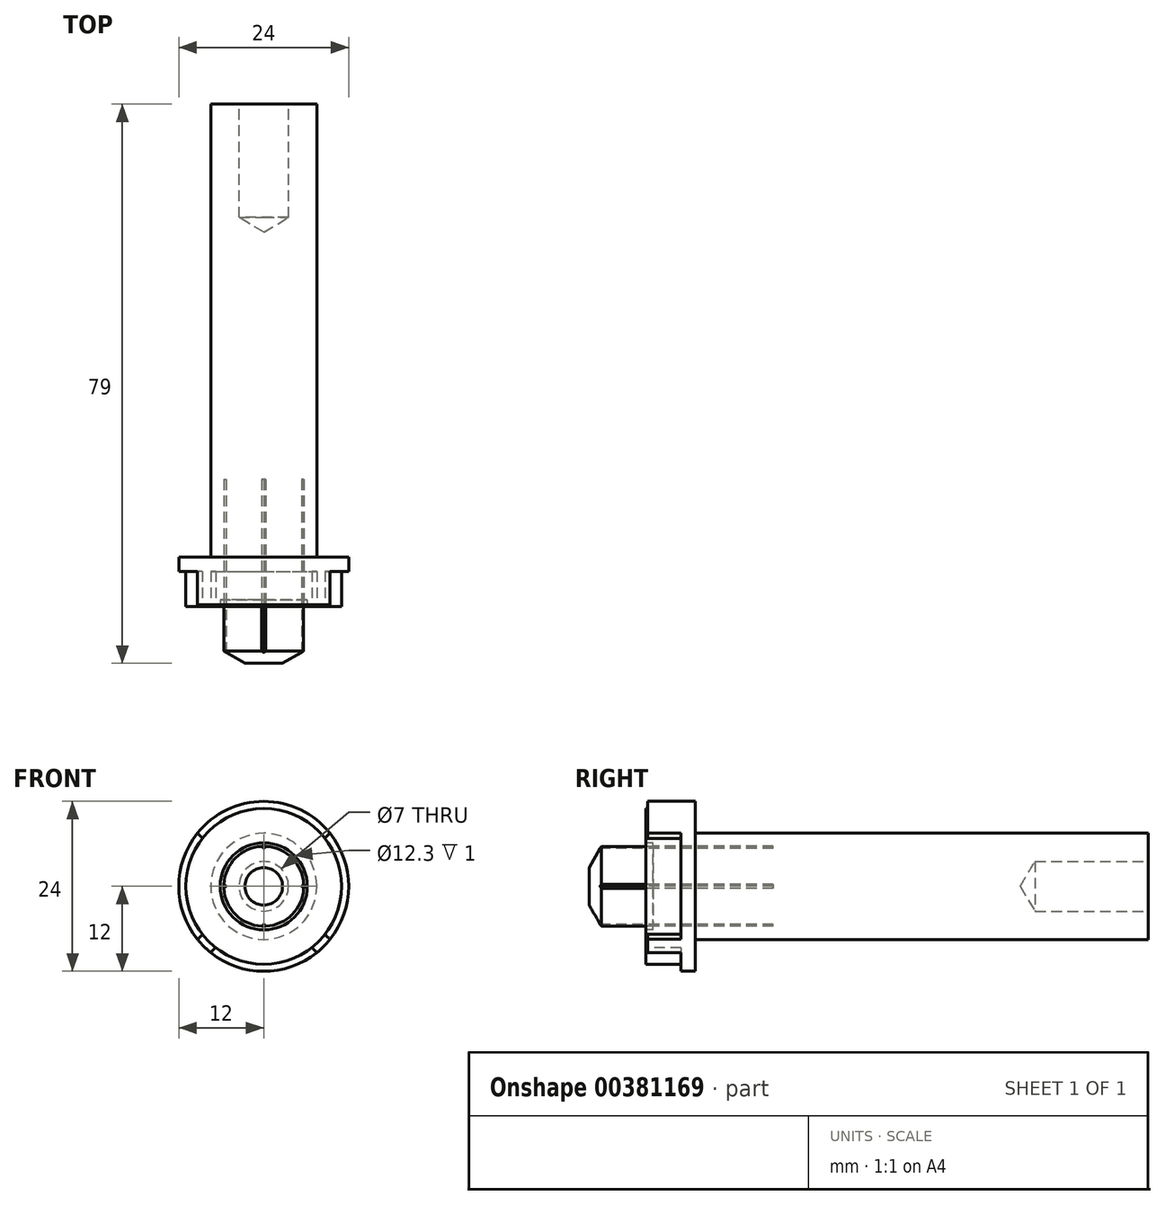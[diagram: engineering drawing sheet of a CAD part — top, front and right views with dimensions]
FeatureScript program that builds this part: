
annotation { "Feature Type Name" : "Feature", "Feature Type Description" : "" }
export const myFeature = defineFeature(function(context is Context, id is Id, definition is map)
    precondition{}
    {
        {
            var Q0;
            Q0=qCreatedBy(makeId("Front.planeOp"),FACE);
            var sketch = newSketch(context, id + "F0", { "sketchPlane" : qUnion([Q0])});
            skCircle(sketch, "E0", {"center": v(0, 0) * mm, "radius": 12 * mm});
            skSolve(sketch);
        }
        {
            var Q0;
            Q0=makeQuery(id+"F0.imprint","IMPRINT",FACE,{"disambiguationData":[TD([[makeQuery(id+"F0.imprint","IMPRINT",EDGE,{"derivedFrom":sQuery(id+"F0.wireOp",EDGE,"E0")}),1.0]])]});
            extrude(context, id + "F1", {"entities" : qUnion([Q0]), "depth" : 7 * mm});
        }
        {
            var Q0;
            Q0=makeQuery(id+"F1.opExtrude","CAP_FACE",FACE,{"disambiguationData":[OSD([sQuery(id+"F0.wireOp",EDGE,"E0")])],"isStart":true});
            var sketch = newSketch(context, id + "F2", { "sketchPlane" : qUnion([Q0])});
            skCircle(sketch, "E1", {"center": v(0, 0) * mm, "radius": 7.5 * mm});
            skSolve(sketch);
        }
        {
            var Q0;
            Q0=makeQuery(id+"F2.imprint","IMPRINT",FACE,{"disambiguationData":[TD([[makeQuery(id+"F2.imprint","IMPRINT",EDGE,{"derivedFrom":sQuery(id+"F2.wireOp",EDGE,"E1")}),1.0]])]});
            extrude(context, id + "F3", {"entities" : qUnion([Q0]), "operationType" : NewBodyOperationType.ADD, "depth" : 64 * mm});
        }
        {
            var Q0;
            Q0=makeQuery(id+"F3.opExtrude","CAP_FACE",FACE,{"disambiguationData":[OSD([sQuery(id+"F2.wireOp",EDGE,"E1")])],"isStart":false});
            var sketch = newSketch(context, id + "F4", { "sketchPlane" : qUnion([Q0])});
            skPoint(sketch, "E2", {"position": v(0, 0) * mm});
            skSolve(sketch);
        }
        {
            var Q0;
            Q0=sQuery(id+"F4.wireOp",VERTEX,"E2");
            var Q1;
            Q1=makeQuery(id+"F1.opExtrude","SWEPT_BODY",BODY,{"disambiguationData":[OSD([sQuery(id+"F0.wireOp",EDGE,"E0")])]});
            hole(context, id + "F5", {"style" : HoleStyle.SIMPLE, "endStyle" : HoleEndStyle.BLIND, "standardTappedOrClearance" : lookupTablePath({ "standard" : "ISO", "engagement" : "75%", "pitch" : "1 mm", "size" : "M8", "type" : "Tapped" }), "standardBlindInLast" : lookupTablePath({ "standard" : "ISO", "engagement" : "75%", "pitch" : "1 mm", "size" : "M8", "type" : "Tapped" }), "holeDiameter" : 7 * mm, "showTappedDepth" : true, "holeDepth" : 16 * mm, "isTappedThrough" : true, "tappedDepth" : 13 * mm, "tapClearance" : 3, "locations" : qUnion([Q0]), "scope" : qUnion([Q1]), "majorDiameter" : 8 * mm});
        }
        {
            var Q0;
            Q0=makeQuery(id+"F1.opExtrude","CAP_FACE",FACE,{"disambiguationData":[OSD([sQuery(id+"F0.wireOp",EDGE,"E0")])],"isStart":false});
            var sketch = newSketch(context, id + "F6", { "sketchPlane" : qUnion([Q0])});
            skCircle(sketch, "E3", {"center": v(0, 0) * mm, "radius": 11 * mm});
            skSolve(sketch);
        }
        {
            var Q0;
            Q0=makeQuery(id+"F6.imprint","IMPRINT",FACE,{"disambiguationData":[TD([[makeQuery(id+"F6.imprint","IMPRINT",EDGE,{"derivedFrom":sQuery(id+"F6.wireOp",EDGE,"E3")}),-1.0]])]});
            extrude(context, id + "F7", {"entities" : qUnion([Q0]), "operationType" : NewBodyOperationType.REMOVE, "oppositeDirection" : true, "depth" : .3 * mm});
        }
        {
            var Q0;
            Q0=makeQuery(id+"F1.opExtrude","CAP_FACE",FACE,{"disambiguationData":[OSD([sQuery(id+"F0.wireOp",EDGE,"E0")])],"isStart":false});
            var sketch = newSketch(context, id + "F8", { "sketchPlane" : qUnion([Q0])});
            skCircle(sketch, "E4", {"center": v(0, 0) * mm, "radius": 5.65 * mm});
            skSolve(sketch);
        }
        {
            var Q0;
            Q0=makeQuery(id+"F8.imprint","IMPRINT",FACE,{"disambiguationData":[TD([[makeQuery(id+"F8.imprint","IMPRINT",EDGE,{"derivedFrom":sQuery(id+"F8.wireOp",EDGE,"E4")}),1.0]])]});
            extrude(context, id + "F9", {"entities" : qUnion([Q0]), "operationType" : NewBodyOperationType.ADD, "depth" : 8 * mm});
        }
        {
            var Q0;
            Q0=makeQuery(id+"F9.opExtrude","CAP_EDGE",EDGE,{"disambiguationData":[OSD([sQuery(id+"F8.wireOp",EDGE,"E4")])],"isStart":false});
            chamfer(context, id + "F10", {"entities" : qUnion([Q0]), "chamferType" : ChamferType.OFFSET_ANGLE, "width" : 3 * mm, "oppositeDirection" : false, "angle" : 30 * degree, "tangentPropagation" : true});
        }
        {
            var Q0;
            Q0=makeQuery(id+"F1.opExtrude","CAP_FACE",FACE,{"disambiguationData":[OSD([sQuery(id+"F0.wireOp",EDGE,"E0")])],"isStart":false});
            var sketch = newSketch(context, id + "F11", { "sketchPlane" : qUnion([Q0])});
            skCircle(sketch, "E5", {"center": v(0, 0) * mm, "radius": 6.15 * mm});
            skCircle(sketch, "E6", {"center": v(0, 0) * mm, "radius": 5.65 * mm});
            skSolve(sketch);
        }
        {
            var Q0;
            Q0=makeQuery(id+"F11.imprint","IMPRINT",FACE,{"disambiguationData":[TD([[makeQuery(id+"F11.imprint","IMPRINT",EDGE,{"derivedFrom":sQuery(id+"F11.wireOp",EDGE,"E5")}),1.0]])]});
            extrude(context, id + "F12", {"entities" : qUnion([Q0]), "operationType" : NewBodyOperationType.REMOVE, "oppositeDirection" : true, "depth" : 1 * mm});
        }
        {
            var Q0;
            Q0=makeQuery(id+"F1.opExtrude","CAP_FACE",FACE,{"disambiguationData":[OSD([sQuery(id+"F0.wireOp",EDGE,"E0")])],"isStart":false});
            var sketch = newSketch(context, id + "F13", { "sketchPlane" : qUnion([Q0])});
            skArc(sketch, "E7", {"start": v(7.5, -9.4) * mm, "mid": v(0, -6) * mm, "end": v(-7.5, -9.39) * mm});
            skArc(sketch, "E8.1.0", {"start": v(9.4, 7.5) * mm, "mid": v(6, 0) * mm, "end": v(9.39, -7.5) * mm});
            skArc(sketch, "E8.2.0", {"start": v(-7.5, 9.4) * mm, "mid": v(0, 6) * mm, "end": v(7.5, 9.39) * mm});
            skArc(sketch, "E8.3.0", {"start": v(-9.4, -7.5) * mm, "mid": v(-6, 0) * mm, "end": v(-9.39, 7.5) * mm});
            skPoint(sketch, "E8.center", {"position": v(0, 0) * mm});
            skCircle(sketch, "E9", {"center": v(0, 0) * mm, "radius": 12 * mm});
            skSolve(sketch);
        }
        {
            var Q0;
            {var subQ0=sQuery(id+"F13.wireOp",EDGE,"E9");var subQ1=sQuery(id+"F13.wireOp",EDGE,"E8.3.0");var subQ2=makeQuery(id+"F13.imprint","INTERSECT",VERTEX,{"disambiguationData":[OD(0.0)],"derivedFrom":[subQ1,subQ0]});Q0=makeQuery(id+"F13.imprint","IMPRINT",FACE,{"disambiguationData":[TD([[makeQuery(id+"F13.imprint","IMPRINT",EDGE,{"disambiguationData":[TD([[subQ2,-1.0]])],"derivedFrom":subQ1}),1.0]])]});}
            var Q1;
            {var subQ0=sQuery(id+"F13.wireOp",EDGE,"E8.3.0");var subQ1=makeQuery(id+"F7.boolean.opBoolean","COPY",EDGE,{"derivedFrom":makeQuery(id+"F7.opExtrude","CAP_EDGE",EDGE,{"disambiguationData":[OSD([sQuery(id+"F6.wireOp",EDGE,"E3")])],"isStart":true})});var subQ2=makeQuery(id+"F13.imprint","INTERSECT",VERTEX,{"disambiguationData":[OD(0.0)],"derivedFrom":[subQ1,subQ0]});Q1=makeQuery(id+"F13.imprint","IMPRINT",FACE,{"disambiguationData":[TD([[makeQuery(id+"F13.imprint","IMPRINT",EDGE,{"disambiguationData":[TD([[subQ2,-1.0]])],"derivedFrom":subQ0}),1.0]])]});}
            var Q2;
            {var subQ0=sQuery(id+"F13.wireOp",EDGE,"E8.2.0");var subQ1=makeQuery(id+"F7.boolean.opBoolean","COPY",EDGE,{"derivedFrom":makeQuery(id+"F7.opExtrude","CAP_EDGE",EDGE,{"disambiguationData":[OSD([sQuery(id+"F6.wireOp",EDGE,"E3")])],"isStart":true})});var subQ2=makeQuery(id+"F13.imprint","INTERSECT",VERTEX,{"disambiguationData":[OD(0.0)],"derivedFrom":[subQ1,subQ0]});Q2=makeQuery(id+"F13.imprint","IMPRINT",FACE,{"disambiguationData":[TD([[makeQuery(id+"F13.imprint","IMPRINT",EDGE,{"disambiguationData":[TD([[subQ2,-1.0]])],"derivedFrom":subQ0}),1.0]])]});}
            var Q3;
            {var subQ0=sQuery(id+"F13.wireOp",EDGE,"E9");var subQ1=sQuery(id+"F13.wireOp",EDGE,"E8.2.0");var subQ2=makeQuery(id+"F13.imprint","INTERSECT",VERTEX,{"disambiguationData":[OD(0.0)],"derivedFrom":[subQ1,subQ0]});Q3=makeQuery(id+"F13.imprint","IMPRINT",FACE,{"disambiguationData":[TD([[makeQuery(id+"F13.imprint","IMPRINT",EDGE,{"disambiguationData":[TD([[subQ2,-1.0]])],"derivedFrom":subQ1}),1.0]])]});}
            var Q4;
            {var subQ0=sQuery(id+"F13.wireOp",EDGE,"E8.1.0");var subQ1=makeQuery(id+"F7.boolean.opBoolean","COPY",EDGE,{"derivedFrom":makeQuery(id+"F7.opExtrude","CAP_EDGE",EDGE,{"disambiguationData":[OSD([sQuery(id+"F6.wireOp",EDGE,"E3")])],"isStart":true})});var subQ2=makeQuery(id+"F13.imprint","INTERSECT",VERTEX,{"disambiguationData":[OD(0.0)],"derivedFrom":[subQ1,subQ0]});Q4=makeQuery(id+"F13.imprint","IMPRINT",FACE,{"disambiguationData":[TD([[makeQuery(id+"F13.imprint","IMPRINT",EDGE,{"disambiguationData":[TD([[subQ2,-1.0]])],"derivedFrom":subQ0}),1.0]])]});}
            var Q5;
            {var subQ0=sQuery(id+"F13.wireOp",EDGE,"E9");var subQ1=sQuery(id+"F13.wireOp",EDGE,"E8.1.0");var subQ2=makeQuery(id+"F13.imprint","INTERSECT",VERTEX,{"disambiguationData":[OD(0.0)],"derivedFrom":[subQ1,subQ0]});Q5=makeQuery(id+"F13.imprint","IMPRINT",FACE,{"disambiguationData":[TD([[makeQuery(id+"F13.imprint","IMPRINT",EDGE,{"disambiguationData":[TD([[subQ2,-1.0]])],"derivedFrom":subQ1}),1.0]])]});}
            var Q6;
            {var subQ0=sQuery(id+"F13.wireOp",EDGE,"E7");var subQ1=makeQuery(id+"F7.boolean.opBoolean","COPY",EDGE,{"derivedFrom":makeQuery(id+"F7.opExtrude","CAP_EDGE",EDGE,{"disambiguationData":[OSD([sQuery(id+"F6.wireOp",EDGE,"E3")])],"isStart":true})});var subQ2=makeQuery(id+"F13.imprint","INTERSECT",VERTEX,{"disambiguationData":[OD(0.0)],"derivedFrom":[subQ1,subQ0]});Q6=makeQuery(id+"F13.imprint","IMPRINT",FACE,{"disambiguationData":[TD([[makeQuery(id+"F13.imprint","IMPRINT",EDGE,{"disambiguationData":[TD([[subQ2,-1.0]])],"derivedFrom":subQ0}),1.0]])]});}
            var Q7;
            {var subQ0=sQuery(id+"F13.wireOp",EDGE,"E9");var subQ1=sQuery(id+"F13.wireOp",EDGE,"E7");var subQ2=makeQuery(id+"F13.imprint","INTERSECT",VERTEX,{"disambiguationData":[OD(0.0)],"derivedFrom":[subQ1,subQ0]});Q7=makeQuery(id+"F13.imprint","IMPRINT",FACE,{"disambiguationData":[TD([[makeQuery(id+"F13.imprint","IMPRINT",EDGE,{"disambiguationData":[TD([[subQ2,-1.0]])],"derivedFrom":subQ1}),1.0]])]});}
            extrude(context, id + "F14", {"entities" : qUnion([Q0, Q1, Q2, Q3, Q4, Q5, Q6, Q7]), "operationType" : NewBodyOperationType.REMOVE, "oppositeDirection" : true, "depth" : 5 * mm});
        }
        {
            var Q0;
            Q0=makeQuery(id+"F9.opExtrude","CAP_FACE",FACE,{"disambiguationData":[OSD([sQuery(id+"F8.wireOp",EDGE,"E4")])],"isStart":false});
            var sketch = newSketch(context, id + "F15", { "sketchPlane" : qUnion([Q0])});
            skArc(sketch, "E10", {"start": v(0.3, 5.64) * mm, "mid": v(0, 5.65) * mm, "end": v(-0.3, 5.64) * mm});
            skLineSegment(sketch, "E11", {"start": v(-0.3, 5.64) * mm, "end": v(0, 5.34) * mm});
            skLineSegment(sketch, "E12", {"start": v(0, 5.34) * mm, "end": v(0.3, 5.64) * mm});
            skLineSegment(sketch, "E13.1.0", {"start": v(-5.64, -0.3) * mm, "end": v(-5.34, 0) * mm});
            skLineSegment(sketch, "E13.1.1", {"start": v(-5.34, 0) * mm, "end": v(-5.64, 0.3) * mm});
            skArc(sketch, "E13.1.2", {"start": v(-5.64, 0.3) * mm, "mid": v(-5.65, 0) * mm, "end": v(-5.64, -0.3) * mm});
            skLineSegment(sketch, "E13.2.0", {"start": v(0.3, -5.64) * mm, "end": v(0, -5.34) * mm});
            skLineSegment(sketch, "E13.2.1", {"start": v(0, -5.34) * mm, "end": v(-0.3, -5.64) * mm});
            skArc(sketch, "E13.2.2", {"start": v(-0.3, -5.64) * mm, "mid": v(0, -5.65) * mm, "end": v(0.3, -5.64) * mm});
            skLineSegment(sketch, "E13.3.0", {"start": v(5.64, 0.3) * mm, "end": v(5.34, 0) * mm});
            skLineSegment(sketch, "E13.3.1", {"start": v(5.34, 0) * mm, "end": v(5.64, -0.3) * mm});
            skArc(sketch, "E13.3.2", {"start": v(5.64, -0.3) * mm, "mid": v(5.65, 0) * mm, "end": v(5.64, 0.3) * mm});
            skSolve(sketch);
        }
        {
            var Q0;
            Q0=makeQuery(id+"F15.imprint","IMPRINT",FACE,{"disambiguationData":[TD([[makeQuery(id+"F15.imprint","IMPRINT",EDGE,{"derivedFrom":sQuery(id+"F15.wireOp",EDGE,"E10")}),1.0]])]});
            var Q1;
            Q1=makeQuery(id+"F15.imprint","IMPRINT",FACE,{"disambiguationData":[TD([[makeQuery(id+"F15.imprint","IMPRINT",EDGE,{"derivedFrom":sQuery(id+"F15.wireOp",EDGE,"E13.1.0")}),1.0]])]});
            var Q2;
            Q2=makeQuery(id+"F15.imprint","IMPRINT",FACE,{"disambiguationData":[TD([[makeQuery(id+"F15.imprint","IMPRINT",EDGE,{"derivedFrom":sQuery(id+"F15.wireOp",EDGE,"E13.2.0")}),1.0]])]});
            var Q3;
            Q3=makeQuery(id+"F15.imprint","IMPRINT",FACE,{"disambiguationData":[TD([[makeQuery(id+"F15.imprint","IMPRINT",EDGE,{"derivedFrom":sQuery(id+"F15.wireOp",EDGE,"E13.3.0")}),1.0]])]});
            extrude(context, id + "F16", {"entities" : qUnion([Q0, Q1, Q2, Q3]), "operationType" : NewBodyOperationType.REMOVE, "oppositeDirection" : true, "depth" : 26 * mm});
        }
    });
